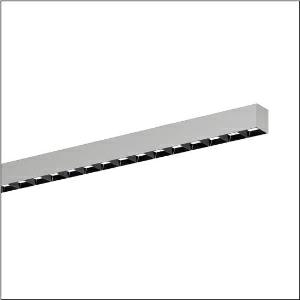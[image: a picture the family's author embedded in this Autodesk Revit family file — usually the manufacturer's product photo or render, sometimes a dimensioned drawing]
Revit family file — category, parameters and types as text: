
# Revit family: silica_r__21_51mx24tat4s_af2d
name_source: partatom
category: Lighting Fixtures
units: mm (PartAtom-declared; Revit-internal decimal feet)

## family parameters
Cut with Voids When Loaded = No
Host = Face
Light Source = No
Part Type = Normal
Room Calculation Point = No
Round Connector Dimension = Use Diameter
Shared = No

## types (1)
- --- (1 x LED, 3280 lm, 32.4 W, 6500K)
    Apparent Load = 32 VA
    CIE Flux Codes = 74 94 99 100 100
    Color Rendering = 80
    Color Temperature = 6500K
    Default Elevation = 1800 mm
    Description = Silica® 21, office luminaire, primary light control with darklight reflector, of PMMA, black, light emission: direct distribution, primary light characteristic: asymmetric, installation type: surface-mounted, LED, rated luminous flux: 3.280lm, luminous efficacy: 96lm/W, light colour: 8tw, colour temperature: 2700..6500K, control gear: ECG DALI, with terminal, 3+2-pole, max. 2.5mm², mains connection: 220..240V, AC, 50/60Hz, rated input power: 34.1W, luminaire housing, of aluminium, metallic grey (RAL 9006), length: 1.204mm, width: 53mm, height: 53mm, protection rating (complete): IP20, insulation class (complete): insulation class I (protective earthing), certification: CE, permissible operating ambient temperature: 0..+35°C, standard: EN 50419, packaging unit: 1 piece
    Height = 0 mm  [stored 0 ft]
    Lamp = 1 x LED
    Lamp Light Flux = 3280 lm
    Lamp Power = 32.4 W
    Lamp count = 1
    Length = 1204 mm
    Luminous efficacy = 101 lm/W
    Manufacturer = Siteco
    ModVariant = No
    Model = 51MX24TAT4S
    Mounting Place = Ceiling
    Mounting Type = Recessed
    Number of Poles = 1
    OnlyDefault = Yes
    Power Factor = 1
    Product Name = Silica® 21
    Product group = office luminaire | ceiling recessed
    ProductGroupID = 401
    Protection Class = Protection class I
    Protection Degree = IP 20
    RLX_Detail_Level = 1
    RLX_Emergency_Light_Flux = 0 lm
    RLX_Emergency_Type = 0
    RLX_Emergency_Type_DB = No
    RlxData = <blob elided: 39729 chars, md5=5a820cc6>
    Socket = socket
    Standby Power = 0 W
    System Light Flux = 3280 lm
    System Power = 32 W
    Type Comments = individual setting
    Type Image = l_1297764.jpg
    URL = http://relux.com
    VarID = @adj_071305
    Voltage = 0 V
    Weight = 0.00 kg
    Width = 53 mm

note: [stored X ft] marks values corroborated as IEEE doubles in the binary element streams (Revit-internal decimal feet)

## geometry (parser evidence)
native form markers: Blend x4, Sweep x9
no freeform markers — native parametric forms only
